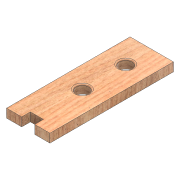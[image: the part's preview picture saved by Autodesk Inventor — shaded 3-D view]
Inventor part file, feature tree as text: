
AUTODESK INVENTOR PART (.ipt)
format: ipt  version: 2018 (Build 220112000, 112)  size: 153,600 bytes
history: native  units: mm
features: sketch x4, extrude x3, fillet x1, projected_geometry x1
ambient origin geometry x8: Origin, YZ Plane, XZ Plane, XY Plane, X Axis, Y Axis, Z Axis, Center Point
bodies: Solid1 (feature_tree)
feature tree (9):
  extrude  "Extrusion1"  Depth=285.0mm
  extrude  "Extrusion2"  Depth=30.0mm
  extrude  "Extrusion3"  Depth=100.0mm
  sketch  "Sketch4"  dims[d10=20.0mm d11=0.0mm d12=20.0mm d13=30.0mm d14=35.0mm d15=10.0mm d16=0.0mm d17=60.0mm d18=100.0mm d19=45.0deg d22=3.0mm]
  fillet  "Fillet3"  Radius=100.0mm
  sketch  "Sketch1"  dims[d0=100.0mm d1=285.0mm]
  sketch  "Sketch2"  dims[d2=20.0mm d3=0.0mm d5=30.0mm]
  sketch  "Sketch3"  dims[d6=50.0mm d7=50.0mm d9=100.0mm]
  projected_geometry  "Projected Loop1"
